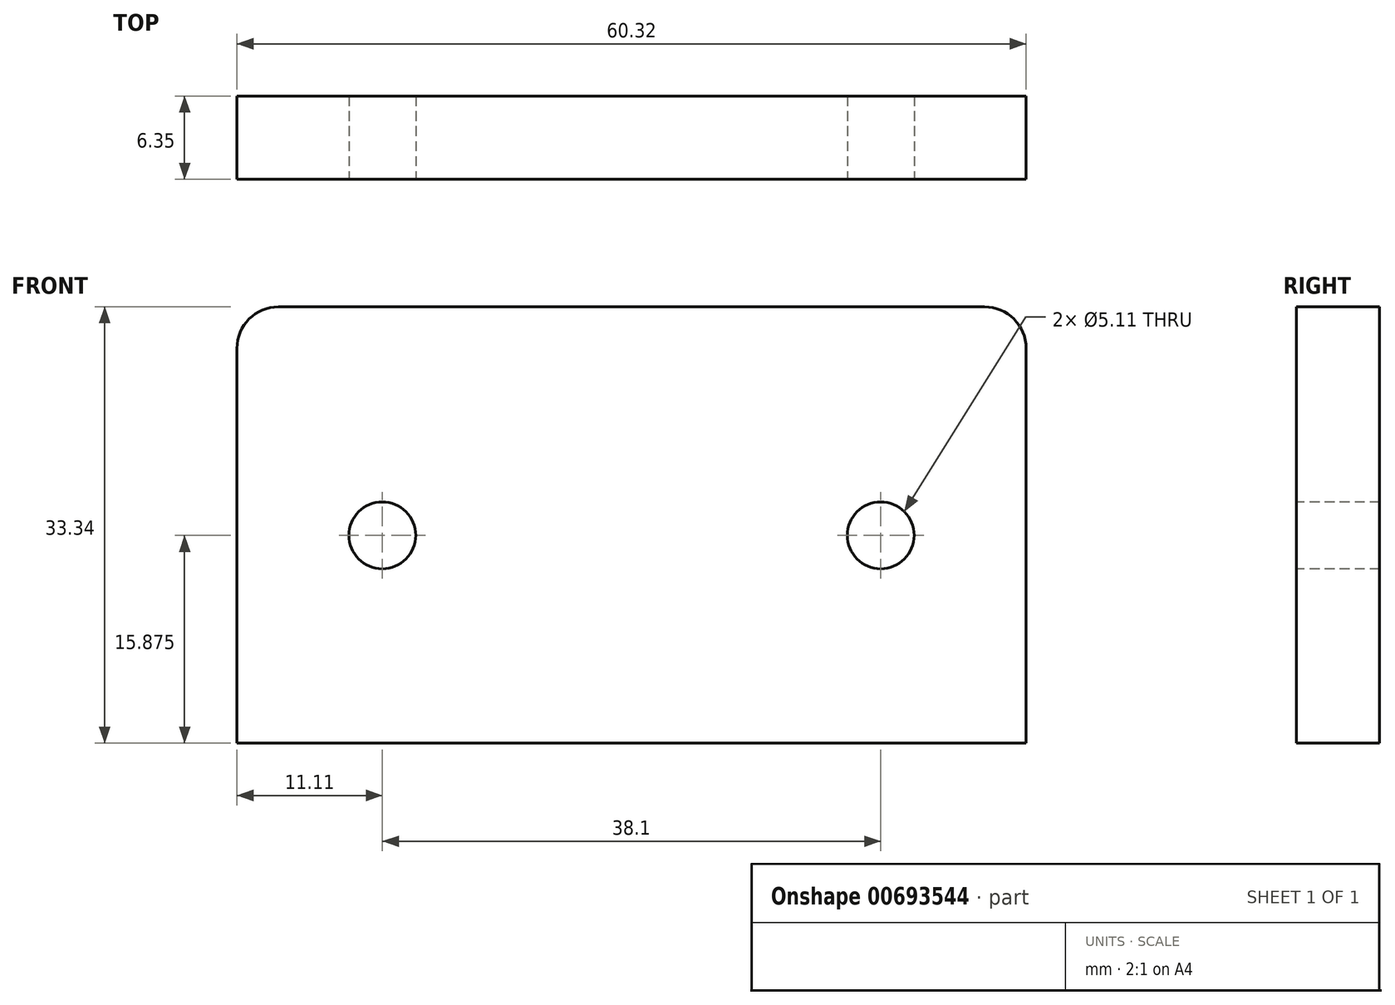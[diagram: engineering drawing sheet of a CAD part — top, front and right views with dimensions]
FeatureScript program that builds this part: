
annotation { "Feature Type Name" : "Feature", "Feature Type Description" : "" }
export const myFeature = defineFeature(function(context is Context, id is Id, definition is map)
    precondition{}
    {
        {
            var Q0;
            Q0=qCreatedBy(makeId("Front.planeOp"),FACE);
            var sketch = newSketch(context, id + "F0", { "sketchPlane" : qUnion([Q0])});
            skLineSegment(sketch, "E0", {"start": v(0, 0) * mm, "end": v(-30.16, 0) * mm});
            skLineSegment(sketch, "E1", {"start": v(-30.16, 0) * mm, "end": v(-30.16, 33.34) * mm});
            skLineSegment(sketch, "E2", {"start": v(-30.16, 33.34) * mm, "end": v(0, 33.34) * mm});
            skLineSegment(sketch, "E3.MirrorCS", {"start": v(0, 0) * mm, "end": v(30.16, 0) * mm});
            skLineSegment(sketch, "E4.MirrorCS", {"start": v(30.16, 33.34) * mm, "end": v(0, 33.34) * mm});
            skLineSegment(sketch, "E5.MirrorCS", {"start": v(30.16, 0) * mm, "end": v(30.16, 33.34) * mm});
            skPoint(sketch, "E6", {"position": v(-19.05, 15.88) * mm});
            skPoint(sketch, "E7.MirrorP", {"position": v(19.05, 15.88) * mm});
            skSolve(sketch);
        }
        {
            var Q0;
            Q0 = qSketchRegion(id + "F0", true);
            extrude(context, id + "F1", {"entities" : qUnion([Q0]), "depth" : 6.35 * mm, "offsetDistance" : 25.4 * mm});
        }
        {
            var Q0;
            Q0=sQuery(id+"F0.wireOp",VERTEX,"E6");
            var Q1;
            Q1=sQuery(id+"F0.wireOp",VERTEX,"E7.MirrorP");
            var Q2;
            Q2=makeQuery(id+"F1.opExtrude","SWEPT_BODY",BODY,{"disambiguationData":[OSD([sQuery(id+"F0.wireOp",EDGE,"E0"),sQuery(id+"F0.wireOp",EDGE,"E1"),sQuery(id+"F0.wireOp",EDGE,"E2"),sQuery(id+"F0.wireOp",EDGE,"E3.MirrorCS"),sQuery(id+"F0.wireOp",EDGE,"E4.MirrorCS"),sQuery(id+"F0.wireOp",EDGE,"E5.MirrorCS")])]});
            hole(context, id + "F2", {"style" : HoleStyle.SIMPLE, "endStyle" : HoleEndStyle.THROUGH, "oppositeDirection" : true, "standardTappedOrClearance" : lookupTablePath({ "standard" : "ANSI", "engagement" : "75%", "pitch" : "20 tpi", "size" : "1/4", "type" : "Tapped" }), "standardBlindInLast" : lookupTablePath({ "standard" : "ANSI", "engagement" : "75%", "pitch" : "20 tpi", "size" : "1/4", "type" : "Tapped" }), "holeDiameter" : 5.1 * mm, "majorDiameter" : 6.35 * mm, "showTappedDepth" : true, "isTappedThrough" : true, "tappedDepth" : 7.14 * mm, "tapClearance" : 3, "locations" : qUnion([Q0, Q1]), "scope" : qUnion([Q2]), "startStyle" : HoleStartStyle.SKETCH});
        }
        {
            var Q0;
            Q0=makeQuery(id+"F1.opExtrude","SWEPT_EDGE",EDGE,{"disambiguationData":[OSD([sQuery(id+"F0.wireOp",EDGE,"E1"),sQuery(id+"F0.wireOp",EDGE,"E2")])]});
            var Q1;
            Q1=makeQuery(id+"F1.opExtrude","SWEPT_EDGE",EDGE,{"disambiguationData":[OSD([sQuery(id+"F0.wireOp",EDGE,"E4.MirrorCS"),sQuery(id+"F0.wireOp",EDGE,"E5.MirrorCS")])]});
            fillet(context, id + "F3", {"entities" : qUnion([Q0, Q1]), "radius" : 3.17 * mm, "tangentPropagation" : true, "allowEdgeOverflow" : false});
        }
    });
